# Revit family: Sechskantmutter DIN EN ISO 4032, fvz
name_source: partatom
category: HLS-Bauteile
revit_build: Autodesk Revit 2017 (Build: 20190507_1515(x64)
units: mm (PartAtom-declared; Revit-internal decimal feet)

## family parameters
Arbeitsebenenbasiert = Ja
Beim Laden mit Abzugskörper schneiden = Nein
Bemaßung runder Anschluss = Durchmesser verwenden
Gemeinsam genutzt = Ja
Immer vertikal = Nein
Raumberechnungspunkt = Nein
Teiletyp = Normal

## types (3) — shared parameters
Fabrikat = MEFA
Firma = MEFA Befestigungs- und Montagesysteme GmbH
Kurztext1 = Sechskantmutter Stahl fvz
Material = Stahl
Mengeneinheit = St
Vorgabe-Ansicht = 1219 mm
vpe = 100 St

## per-type parameters (varying)
| type | Artikelnummer | D | EAN | F2 | Gewicht | Gewicht pro Bauteil | H | Kurztext2 |
| Sechskantmutter M16, fvz | 4120523/fvz | 7 mm  [stored 0.0229659 ft] | 4250928457165 | 12 mm  [stored 0.0393701 ft] | 0.04 kg | 0.04 kg | 13 mm | M16 SW 24 |
| Sechskantmutter M10, fvz | 4120477/fvz | 4 mm  [stored 0.0131234 ft] | 4250928457141 | 9 mm  [stored 0.0295276 ft] | 0.01 kg | 0.01 kg | 8 mm  [stored 0.0262467 ft] | M10 SW 17 |
| Sechskantmutter M12, fvz | 4120485/fvz | 5 mm  [stored 0.0164042 ft] | 4250928457158 | 9 mm  [stored 0.0295276 ft] | 0.02 kg | 0.02 kg | 10 mm  [stored 0.0328084 ft] | M12 SW 19 |

note: [stored X ft] marks values corroborated as IEEE doubles in the binary element streams (Revit-internal decimal feet)

## geometry (parser evidence)
native form markers: Sweep x3
no freeform markers — native parametric forms only
